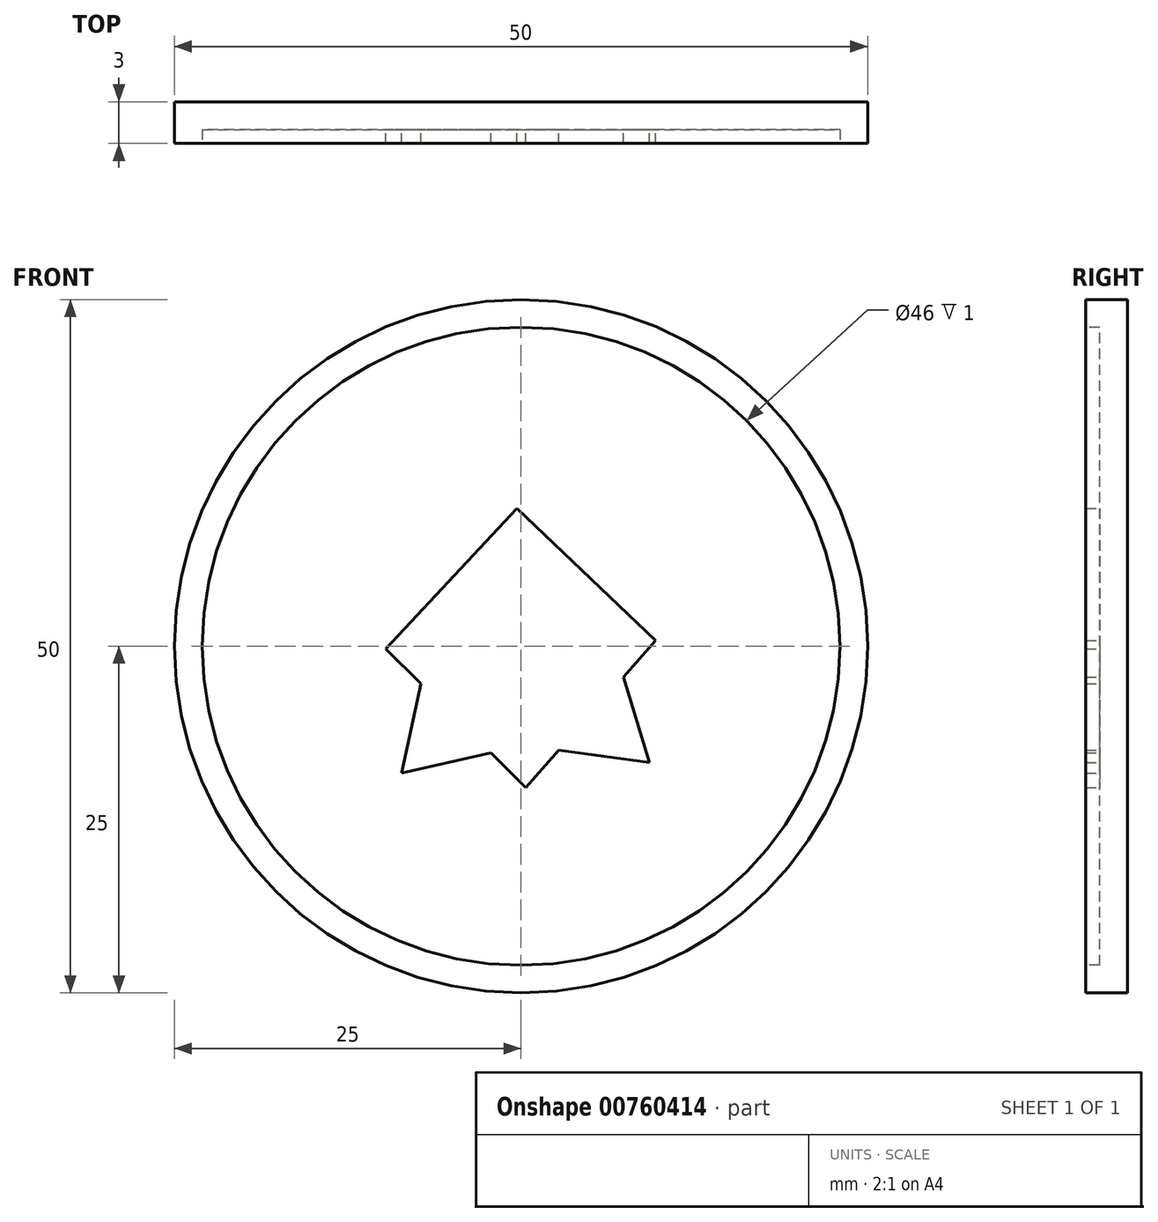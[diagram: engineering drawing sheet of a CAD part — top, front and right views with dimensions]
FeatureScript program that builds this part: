
annotation { "Feature Type Name" : "Feature", "Feature Type Description" : "" }
export const myFeature = defineFeature(function(context is Context, id is Id, definition is map)
    precondition{}
    {
        {
            var Q0;
            Q0=qCreatedBy(makeId("Front.planeOp"),FACE);
            var sketch = newSketch(context, id + "F0", { "sketchPlane" : qUnion([Q0])});
            skCircle(sketch, "E0", {"center": v(0, 0) * mm, "radius": 25 * mm});
            skSolve(sketch);
        }
        {
            var Q0;
            Q0 = qSketchRegion(id + "F0", true);
            extrude(context, id + "F1", {"entities" : qUnion([Q0]), "endBound" : BoundingType.SYMMETRIC, "depth" : 3 * mm, "offsetDistance" : 25 * mm});
        }
        {
            var Q0;
            Q0=makeQuery(id+"F1.opExtrude","CAP_FACE",FACE,{"disambiguationData":[OSD([sQuery(id+"F0.wireOp",EDGE,"E0")])],"isStart":false});
            var sketch = newSketch(context, id + "F2", { "sketchPlane" : qUnion([Q0])});
            skCircle(sketch, "E1", {"center": v(0, 0) * mm, "radius": 23 * mm});
            skSolve(sketch);
        }
        {
            var Q0;
            Q0 = qSketchRegion(id + "F2", true);
            extrude(context, id + "F3", {"entities" : qUnion([Q0]), "operationType" : NewBodyOperationType.REMOVE, "oppositeDirection" : true, "depth" : 1 * mm, "offsetDistance" : 25 * mm});
        }
        {
            var Q0;
            Q0=makeQuery(id+"F3.boolean.opBoolean","COPY",FACE,{"derivedFrom":makeQuery(id+"F3.opExtrude","CAP_FACE",FACE,{"disambiguationData":[OSD([sQuery(id+"F2.wireOp",EDGE,"E1")])],"isStart":false})});
            var sketch = newSketch(context, id + "F4", { "sketchPlane" : qUnion([Q0])});
            skLineSegment(sketch, "E2", {"start": v(-11.04, 20.18) * mm, "end": v(20.7, -10.03) * mm});
            skLineSegment(sketch, "E3", {"start": v(-20.48, 10.48) * mm, "end": v(10.6, -20.4) * mm});
            skLineSegment(sketch, "E4", {"start": v(9.87, 20.78) * mm, "end": v(-20.08, -11.2) * mm});
            skLineSegment(sketch, "E5", {"start": v(19.73, 11.82) * mm, "end": v(-9.23, -21.07) * mm});
            skSolve(sketch);
        }
        {
            var Q0;
            Q0 = qSketchRegion(id + "F4", true);
            extrude(context, id + "F5", {"entities" : qUnion([Q0]), "operationType" : NewBodyOperationType.ADD, "depth" : 1 * mm, "offsetDistance" : 25 * mm});
        }
        {
            var Q0;
            Q0=makeQuery(id+"F3.boolean.opBoolean","COPY",FACE,{"derivedFrom":makeQuery(id+"F3.opExtrude","CAP_FACE",FACE,{"disambiguationData":[OSD([sQuery(id+"F2.wireOp",EDGE,"E1")])],"isStart":false})});
            var sketch = newSketch(context, id + "F6", { "sketchPlane" : qUnion([Q0])});
            skLineSegment(sketch, "E6", {"start": v(2.72, -7.5) * mm, "end": v(9.26, -8.4) * mm});
            skLineSegment(sketch, "E7", {"start": v(9.26, -8.4) * mm, "end": v(7.37, -2.22) * mm});
            skLineSegment(sketch, "E8", {"start": v(2.72, -7.5) * mm, "end": v(7.37, -2.22) * mm});
            skLineSegment(sketch, "E9", {"start": v(-7.23, -2.69) * mm, "end": v(-8.63, -9.14) * mm});
            skLineSegment(sketch, "E10", {"start": v(-8.63, -9.14) * mm, "end": v(-2.19, -7.7) * mm});
            skLineSegment(sketch, "E11", {"start": v(-2.19, -7.7) * mm, "end": v(-7.23, -2.69) * mm});
            skSolve(sketch);
        }
        {
            var Q0;
            Q0 = qSketchRegion(id + "F6", true);
            extrude(context, id + "F7", {"entities" : qUnion([Q0]), "operationType" : NewBodyOperationType.ADD, "depth" : 1 * mm, "offsetDistance" : 25 * mm});
        }
    });
